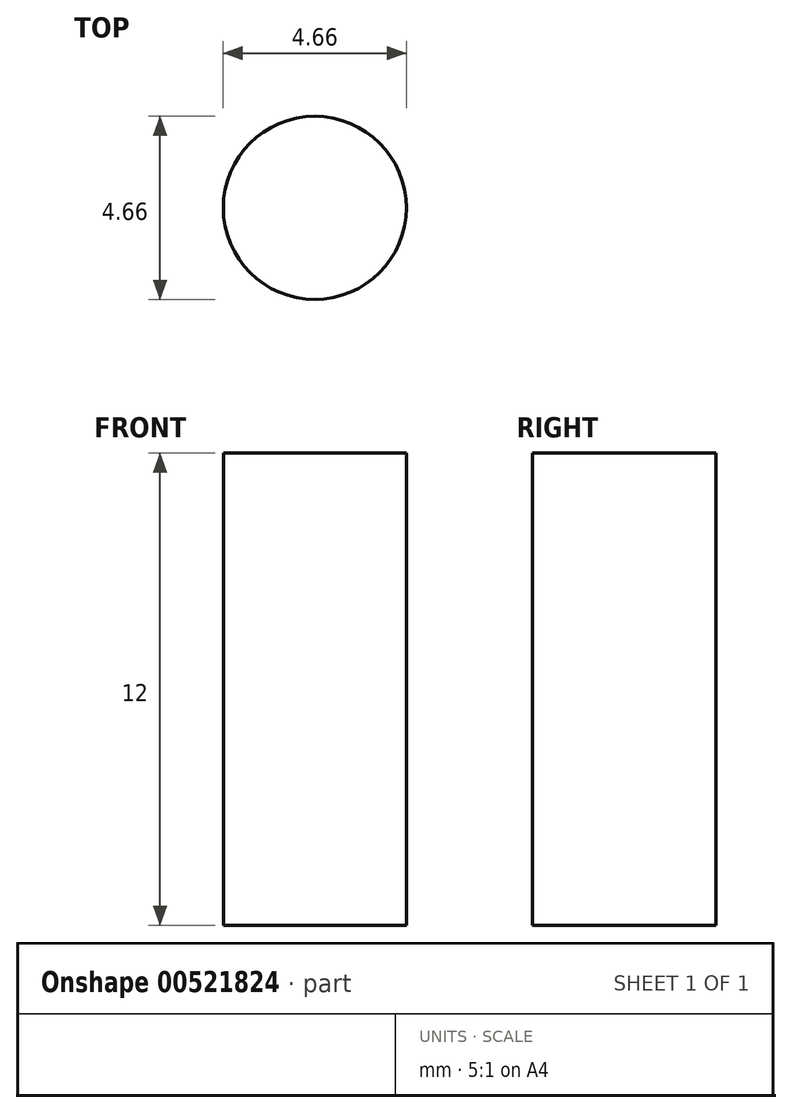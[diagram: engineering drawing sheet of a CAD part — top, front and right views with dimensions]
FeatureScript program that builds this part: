
annotation { "Feature Type Name" : "Feature", "Feature Type Description" : "" }
export const myFeature = defineFeature(function(context is Context, id is Id, definition is map)
    precondition{}
    {
        {
            var Q0;
            Q0=qCreatedBy(makeId("Top.planeOp"),FACE);
            var sketch = newSketch(context, id + "F0", { "sketchPlane" : qUnion([Q0])});
            skCircle(sketch, "E0", {"center": v(0, 0) * mm, "radius": 2.33 * mm});
            skSolve(sketch);
        }
        {
            var Q0;
            Q0 = qSketchRegion(id + "F0", true);
            extrude(context, id + "F1", {"entities" : qUnion([Q0]), "depth" : 12 * mm, "offsetDistance" : 25 * mm});
        }
    });
